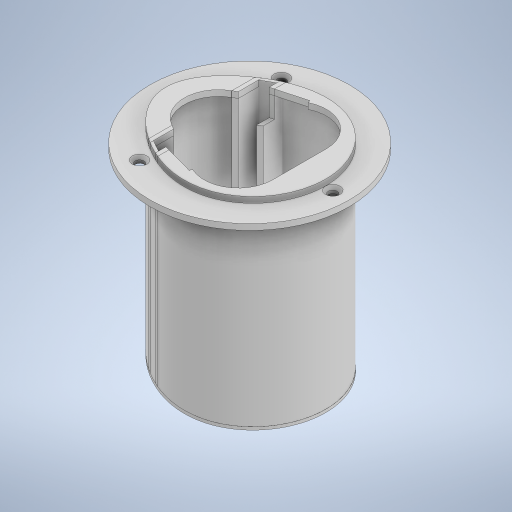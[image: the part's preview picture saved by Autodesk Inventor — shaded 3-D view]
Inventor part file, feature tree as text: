
AUTODESK INVENTOR PART (.ipt)
format: ipt  version: 2023 (Build 270158000, 158)  size: 1,648,128 bytes
history: native  units: mm
features: extrude x14, other x6, chamfer x1, sketch x1
ambient origin geometry x8: Origin, YZ Plane, XZ Plane, XY Plane, X Axis, Y Axis, Z Axis, Center Point
bodies: Volumenkörper6 (feature_tree), Volumenkörper8 (feature_tree), Volumenkörper9 (feature_tree)
feature tree (22):
  other  "Vertikale Skizze"
  extrude  "Hauptkörper oben"  Depth=2.0mm
  extrude  "Hauptkörper unten"  Depth=2.0mm
  extrude  "Bodenkörper"  Depth=2.0mm
  other  "Boden"
  other  "Akkuführungslasche vertikale Skizze"
  extrude  "Akkuführungslasche"  TaperAngle=0.0deg  [1 undecoded]
  extrude  "Akkuführungslasche boolean"  Depth=66.0mm
  extrude  "Extrusion13"  TaperAngle=0.0deg  [1 undecoded]
  extrude  "Akkuführungslasche boolean außen"  Depth=2.0mm
  extrude  "Extrusion15"  TaperAngle=0.0deg  [1 undecoded]
  extrude  "Akkuführungslasche boolean hauptkörper"  TaperAngle=0.0deg  [1 undecoded]
  extrude  "Hauptkörper Außenwand oben"  TaperAngle=0.0deg  [1 undecoded]
  extrude  "Kontaktlöcher"  Depth=68.0mm
  extrude  "Akkuführungslasche boolean2"  TaperAngle=0.0deg  [1 undecoded]
  extrude  "Akkuführungslasche boolean3"  Depth=66.0mm
  extrude  "Halterungsebene"  TaperAngle=0.0deg  [1 undecoded]
  chamfer  "Schraubenlöcherabrundung"  Distance=2.0mm
  other  "Vorlage von oben"
  other  "Bild2"
  sketch  "Skizze8"  dims[d3=68.0mm d4=11.7mm d64=1.0mm d79=2.0mm d80=0.0mm d82=66.0mm d83=0.0mm d86=1.0mm d87=0.0mm d88=0.0mm d89=-66.0mm d90=0.0mm d137=68.0mm d138=0.0mm d140=66.0mm d141=0.0mm d142=2.0mm d143=0.0mm d145=66.0mm d146=0.0mm d147=2.0mm d148=0.0mm d149=2.0mm d150=0.0mm d151=2.0mm d152=0.0mm d182=10.0mm d183=0.0mm d197=7.0mm d198=0.0mm d199=2.0mm d200=0.0mm d207=3.0mm d208=3.0mm d209=3.0mm d212=2.0mm d213=0.0mm d214=1.0mm d215=2.0mm d216=45.0deg d8=0.5mm d9=0.872665mm d10=0.5mm d11=0.872665mm d99=0.5mm d100=0.872665mm d101=0.5mm d102=0.872665mm d139=0.5mm d189=0.5mm d190=0.872665mm d191=0.5mm d192=0.872665mm d193=0.5mm d194=0.872665mm d195=0.5mm d196=0.872665mm]
  other  "Bild3"
note: 7 required parameter values undecoded (feature->parameter linkage not recoverable at this tier; creation-order binding heuristic only, values carry confidence <= 0.55)
